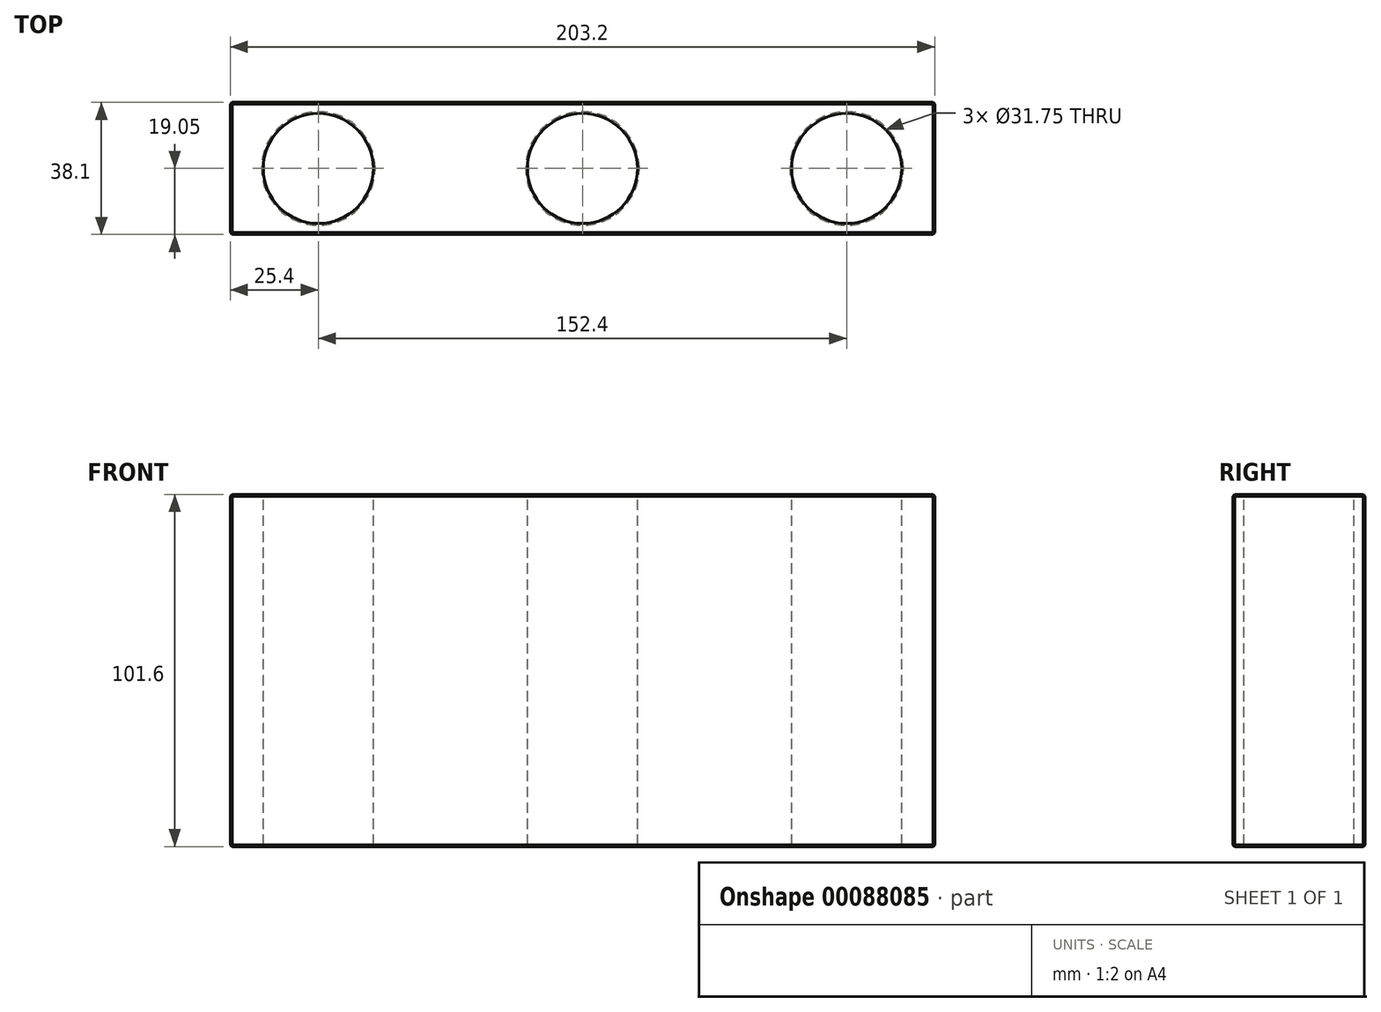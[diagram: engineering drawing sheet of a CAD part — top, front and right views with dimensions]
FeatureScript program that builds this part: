
annotation { "Feature Type Name" : "Feature", "Feature Type Description" : "" }
export const myFeature = defineFeature(function(context is Context, id is Id, definition is map)
    precondition{}
    {
        {
            var Q0;
            Q0=qCreatedBy(makeId("Top.planeOp"),FACE);
            var sketch = newSketch(context, id + "F0", { "sketchPlane" : qUnion([Q0])});
            skLineSegment(sketch, "E0.bottom", {"start": v(0, 0) * mm, "end": v(203.2, 0) * mm});
            skLineSegment(sketch, "E0.top", {"start": v(0, -38.1) * mm, "end": v(203.2, -38.1) * mm});
            skLineSegment(sketch, "E0.left", {"start": v(0, 0) * mm, "end": v(0, -38.1) * mm});
            skLineSegment(sketch, "E0.right", {"start": v(203.2, 0) * mm, "end": v(203.2, -38.1) * mm});
            skSolve(sketch);
        }
        {
            var Q0;
            Q0=makeQuery(id+"F0.imprint","IMPRINT",FACE,{"disambiguationData":[TD([[makeQuery(id+"F0.imprint","IMPRINT",EDGE,{"derivedFrom":sQuery(id+"F0.wireOp",EDGE,"E0.bottom")}),-1.0]])]});
            extrude(context, id + "F1", {"entities" : qUnion([Q0]), "depth" : 101.6 * mm});
        }
        {
            var Q0;
            Q0=makeQuery(id+"F1.opExtrude","CAP_FACE",FACE,{"disambiguationData":[OSD([sQuery(id+"F0.wireOp",EDGE,"E0.bottom"),sQuery(id+"F0.wireOp",EDGE,"E0.top"),sQuery(id+"F0.wireOp",EDGE,"E0.left"),sQuery(id+"F0.wireOp",EDGE,"E0.right")])],"isStart":false});
            var sketch = newSketch(context, id + "F2", { "sketchPlane" : qUnion([Q0])});
            skLineSegment(sketch, "E1", {"start": v(0, -19.05) * mm, "end": v(50.8, -19.05) * mm, "construction": true});
            skLineSegment(sketch, "E2", {"start": v(101.6, 0) * mm, "end": v(101.6, -38.1) * mm, "construction": true});
            skLineSegment(sketch, "E3", {"start": v(50.8, 0) * mm, "end": v(50.8, -38.1) * mm, "construction": true});
            skLineSegment(sketch, "E4.trimOffspring", {"start": v(152.4, -19.05) * mm, "end": v(203.2, -19.05) * mm, "construction": true});
            skLineSegment(sketch, "E5", {"start": v(152.4, 0) * mm, "end": v(152.4, -38.1) * mm, "construction": true});
            skCircle(sketch, "E6", {"center": v(25.4, -19.05) * mm, "radius": 15.88 * mm});
            skCircle(sketch, "E7", {"center": v(177.8, -19.05) * mm, "radius": 15.88 * mm});
            skCircle(sketch, "E8", {"center": v(101.6, -19.05) * mm, "radius": 15.88 * mm});
            skSolve(sketch);
        }
        {
            var Q0;
            Q0 = qSketchRegion(id + "F2", true);
            extrude(context, id + "F3", {"entities" : qUnion([Q0]), "operationType" : NewBodyOperationType.REMOVE, "endBound" : BoundingType.THROUGH_ALL, "oppositeDirection" : true, "depth" : 25.4 * mm});
        }
        {
            var Q0;
            Q0=makeQuery(id+"F1.opExtrude","SWEPT_EDGE",EDGE,{"disambiguationData":[OSD([sQuery(id+"F0.wireOp",EDGE,"E0.bottom"),sQuery(id+"F0.wireOp",EDGE,"E0.right")])]});
            var Q1;
            Q1=makeQuery(id+"F1.opExtrude","SWEPT_EDGE",EDGE,{"disambiguationData":[OSD([sQuery(id+"F0.wireOp",EDGE,"E0.top"),sQuery(id+"F0.wireOp",EDGE,"E0.right")])]});
            var Q2;
            Q2=makeQuery(id+"F1.opExtrude","SWEPT_EDGE",EDGE,{"disambiguationData":[OSD([sQuery(id+"F0.wireOp",EDGE,"E0.bottom"),sQuery(id+"F0.wireOp",EDGE,"E0.left")])]});
            var Q3;
            Q3=makeQuery(id+"F1.opExtrude","SWEPT_EDGE",EDGE,{"disambiguationData":[OSD([sQuery(id+"F0.wireOp",EDGE,"E0.top"),sQuery(id+"F0.wireOp",EDGE,"E0.left")])]});
            var Q4;
            Q4=makeQuery(id+"F1.opExtrude","CAP_EDGE",EDGE,{"disambiguationData":[OSD([sQuery(id+"F0.wireOp",EDGE,"E0.top")])],"isStart":false});
            var Q5;
            Q5=makeQuery(id+"F1.opExtrude","CAP_EDGE",EDGE,{"disambiguationData":[OSD([sQuery(id+"F0.wireOp",EDGE,"E0.left")])],"isStart":false});
            var Q6;
            Q6=makeQuery(id+"F1.opExtrude","CAP_EDGE",EDGE,{"disambiguationData":[OSD([sQuery(id+"F0.wireOp",EDGE,"E0.bottom")])],"isStart":false});
            var Q7;
            Q7=makeQuery(id+"F1.opExtrude","CAP_EDGE",EDGE,{"disambiguationData":[OSD([sQuery(id+"F0.wireOp",EDGE,"E0.top")])],"isStart":true});
            var Q8;
            Q8=makeQuery(id+"F1.opExtrude","CAP_EDGE",EDGE,{"disambiguationData":[OSD([sQuery(id+"F0.wireOp",EDGE,"E0.bottom")])],"isStart":true});
            var Q9;
            Q9=makeQuery(id+"F1.opExtrude","CAP_EDGE",EDGE,{"disambiguationData":[OSD([sQuery(id+"F0.wireOp",EDGE,"E0.left")])],"isStart":true});
            var Q10;
            Q10=makeQuery(id+"F1.opExtrude","CAP_EDGE",EDGE,{"disambiguationData":[OSD([sQuery(id+"F0.wireOp",EDGE,"E0.right")])],"isStart":true});
            var Q11;
            Q11=makeQuery(id+"F1.opExtrude","CAP_EDGE",EDGE,{"disambiguationData":[OSD([sQuery(id+"F0.wireOp",EDGE,"E0.right")])],"isStart":false});
            var Q12;
            Q12=makeQuery(id+"F3.boolean.opBoolean","COPY",EDGE,{"derivedFrom":makeQuery(id+"F3.opExtrude","CAP_EDGE",EDGE,{"disambiguationData":[OSD([sQuery(id+"F2.wireOp",EDGE,"E7")])],"isStart":true})});
            var Q13;
            Q13=makeQuery(id+"F3.boolean.opBoolean","COPY",EDGE,{"derivedFrom":makeQuery(id+"F3.opExtrude","CAP_EDGE",EDGE,{"disambiguationData":[OSD([sQuery(id+"F2.wireOp",EDGE,"E8")])],"isStart":true})});
            var Q14;
            Q14=makeQuery(id+"F3.boolean.opBoolean","COPY",EDGE,{"derivedFrom":makeQuery(id+"F3.opExtrude","CAP_EDGE",EDGE,{"disambiguationData":[OSD([sQuery(id+"F2.wireOp",EDGE,"E6")])],"isStart":true})});
            var Q15;
            Q15=makeQuery(id+"F3.boolean.opBoolean","INTERSECT",EDGE,{"derivedFrom":[makeQuery(id+"F1.opExtrude","CAP_FACE",FACE,{"disambiguationData":[OSD([sQuery(id+"F0.wireOp",EDGE,"E0.bottom"),sQuery(id+"F0.wireOp",EDGE,"E0.top"),sQuery(id+"F0.wireOp",EDGE,"E0.left"),sQuery(id+"F0.wireOp",EDGE,"E0.right")])],"isStart":true}),makeQuery(id+"F3.opExtrude","SWEPT_FACE",FACE,{"disambiguationData":[OSD([sQuery(id+"F2.wireOp",EDGE,"E6")])]})]});
            var Q16;
            Q16=makeQuery(id+"F3.boolean.opBoolean","INTERSECT",EDGE,{"derivedFrom":[makeQuery(id+"F1.opExtrude","CAP_FACE",FACE,{"disambiguationData":[OSD([sQuery(id+"F0.wireOp",EDGE,"E0.bottom"),sQuery(id+"F0.wireOp",EDGE,"E0.top"),sQuery(id+"F0.wireOp",EDGE,"E0.left"),sQuery(id+"F0.wireOp",EDGE,"E0.right")])],"isStart":true}),makeQuery(id+"F3.opExtrude","SWEPT_FACE",FACE,{"disambiguationData":[OSD([sQuery(id+"F2.wireOp",EDGE,"E8")])]})]});
            var Q17;
            Q17=makeQuery(id+"F3.boolean.opBoolean","INTERSECT",EDGE,{"derivedFrom":[makeQuery(id+"F1.opExtrude","CAP_FACE",FACE,{"disambiguationData":[OSD([sQuery(id+"F0.wireOp",EDGE,"E0.bottom"),sQuery(id+"F0.wireOp",EDGE,"E0.top"),sQuery(id+"F0.wireOp",EDGE,"E0.left"),sQuery(id+"F0.wireOp",EDGE,"E0.right")])],"isStart":true}),makeQuery(id+"F3.opExtrude","SWEPT_FACE",FACE,{"disambiguationData":[OSD([sQuery(id+"F2.wireOp",EDGE,"E7")])]})]});
            chamfer(context, id + "F4", {"entities" : qUnion([Q0, Q1, Q2, Q3, Q4, Q5, Q6, Q7, Q8, Q9, Q10, Q11, Q12, Q13, Q14, Q15, Q16, Q17]), "width" : 0.5 * mm, "tangentPropagation" : true});
        }
    });
